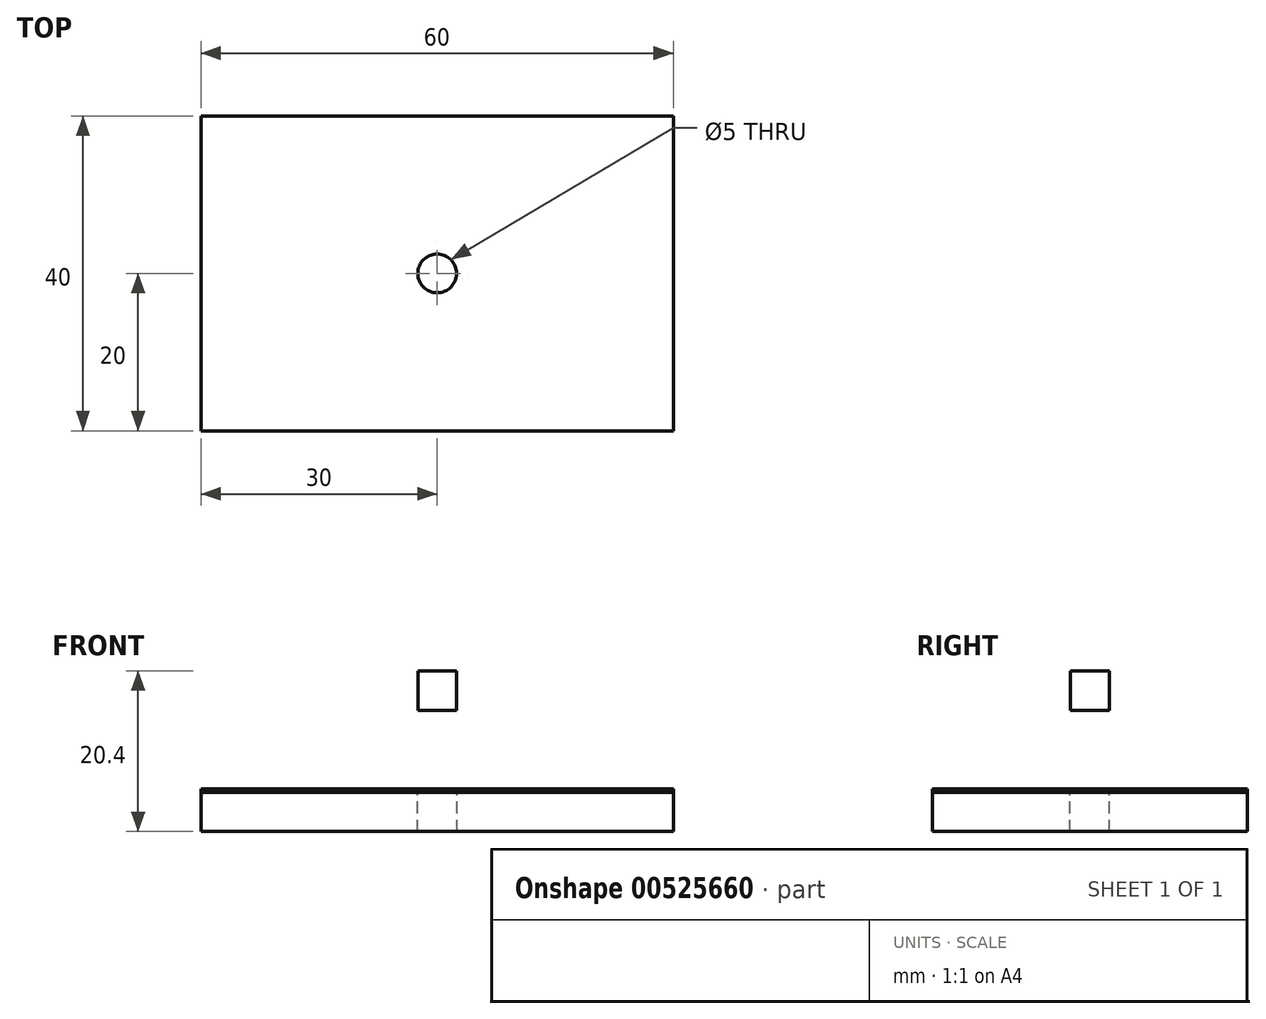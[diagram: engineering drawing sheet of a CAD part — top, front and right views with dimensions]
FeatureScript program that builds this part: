
annotation { "Feature Type Name" : "Feature", "Feature Type Description" : "" }
export const myFeature = defineFeature(function(context is Context, id is Id, definition is map)
    precondition{}
    {
        {
            var Q0;
            Q0=qCreatedBy(makeId("Top.planeOp"),FACE);
            var sketch = newSketch(context, id + "F0", { "sketchPlane" : qUnion([Q0])});
            skLineSegment(sketch, "E0.bottom", {"start": v(-30, -20) * mm, "end": v(30, -20) * mm});
            skLineSegment(sketch, "E0.top", {"start": v(-30, 20) * mm, "end": v(30, 20) * mm});
            skLineSegment(sketch, "E0.left", {"start": v(-30, -20) * mm, "end": v(-30, 20) * mm});
            skLineSegment(sketch, "E0.right", {"start": v(30, -20) * mm, "end": v(30, 20) * mm});
            skSolve(sketch);
        }
        {
            var Q0;
            Q0=makeQuery(id+"F0.imprint","IMPRINT",FACE,{"disambiguationData":[TD([[makeQuery(id+"F0.imprint","IMPRINT",EDGE,{"derivedFrom":sQuery(id+"F0.wireOp",EDGE,"E0.bottom")}),1.0]])]});
            extrude(context, id + "F1", {"entities" : qUnion([Q0]), "oppositeDirection" : true, "depth" : 0.4 * mm, "offsetDistance" : 25 * mm});
        }
        {
            var Q0;
            Q0=qCreatedBy(makeId("Top.planeOp"),FACE);
            cPlane(context, id + "F2", {"entities" : qUnion([Q0]), "cplaneType" : CPlaneType.OFFSET, "offset" : 10 * mm, "width" : 150 * mm, "height" : 150 * mm});
        }
        {
            var Q0;
            Q0=qCreatedBy(id+"F2.planeOp",FACE);
            var sketch = newSketch(context, id + "F3", { "sketchPlane" : qUnion([Q0])});
            skLineSegment(sketch, "E1.0.0", {"start": v(30, 20) * mm, "end": v(-30, 20) * mm, "construction": true});
            skLineSegment(sketch, "E1.0.1", {"start": v(-30, 20) * mm, "end": v(-30, -20) * mm, "construction": true});
            skLineSegment(sketch, "E1.0.2", {"start": v(-30, -20) * mm, "end": v(30, -20) * mm, "construction": true});
            skLineSegment(sketch, "E1.0.3", {"start": v(30, -20) * mm, "end": v(30, 20) * mm, "construction": true});
            skCircle(sketch, "E2", {"center": v(0, 0) * mm, "radius": 2.46 * mm});
            skSolve(sketch);
        }
        {
            var Q0;
            Q0=makeQuery(id+"F3.imprint","IMPRINT",FACE,{"disambiguationData":[TD([[makeQuery(id+"F3.imprint","IMPRINT",EDGE,{"derivedFrom":sQuery(id+"F3.wireOp",EDGE,"E2")}),1.0]])]});
            extrude(context, id + "F4", {"entities" : qUnion([Q0]), "depth" : 5 * mm, "offsetDistance" : 25 * mm});
        }
        {
            var Q0;
            Q0=makeQuery(id+"F1.opExtrude","CAP_FACE",FACE,{"disambiguationData":[OSD([sQuery(id+"F0.wireOp",EDGE,"E0.bottom"),sQuery(id+"F0.wireOp",EDGE,"E0.top"),sQuery(id+"F0.wireOp",EDGE,"E0.left"),sQuery(id+"F0.wireOp",EDGE,"E0.right")])],"isStart":false});
            var sketch = newSketch(context, id + "F5", { "sketchPlane" : qUnion([Q0])});
            skLineSegment(sketch, "E3.0.0", {"start": v(-30, -20) * mm, "end": v(30, -20) * mm});
            skLineSegment(sketch, "E3.0.1", {"start": v(30, -20) * mm, "end": v(30, 20) * mm});
            skLineSegment(sketch, "E3.0.2", {"start": v(30, 20) * mm, "end": v(-30, 20) * mm});
            skLineSegment(sketch, "E3.0.3", {"start": v(-30, 20) * mm, "end": v(-30, -20) * mm});
            skCircle(sketch, "E4.0", {"center": v(0, 0) * mm, "radius": 2.46 * mm, "construction": true});
            skCircle(sketch, "E5", {"center": v(0, 0) * mm, "radius": 2.5 * mm});
            skSolve(sketch);
        }
        {
            var Q0;
            Q0=makeQuery(id+"F5.imprint","IMPRINT",FACE,{"disambiguationData":[TD([[makeQuery(id+"F5.imprint","IMPRINT",EDGE,{"derivedFrom":sQuery(id+"F5.wireOp",EDGE,"E3.0.0")}),1.0]])]});
            var Q1;
            Q1=sQuery(id+"F5.wireOp",EDGE,"E4.0");
            extrude(context, id + "F6", {"entities" : qUnion([Q0]), "surfaceEntities" : qUnion([Q1]), "depth" : 5 * mm, "offsetDistance" : 25 * mm});
        }
    });
